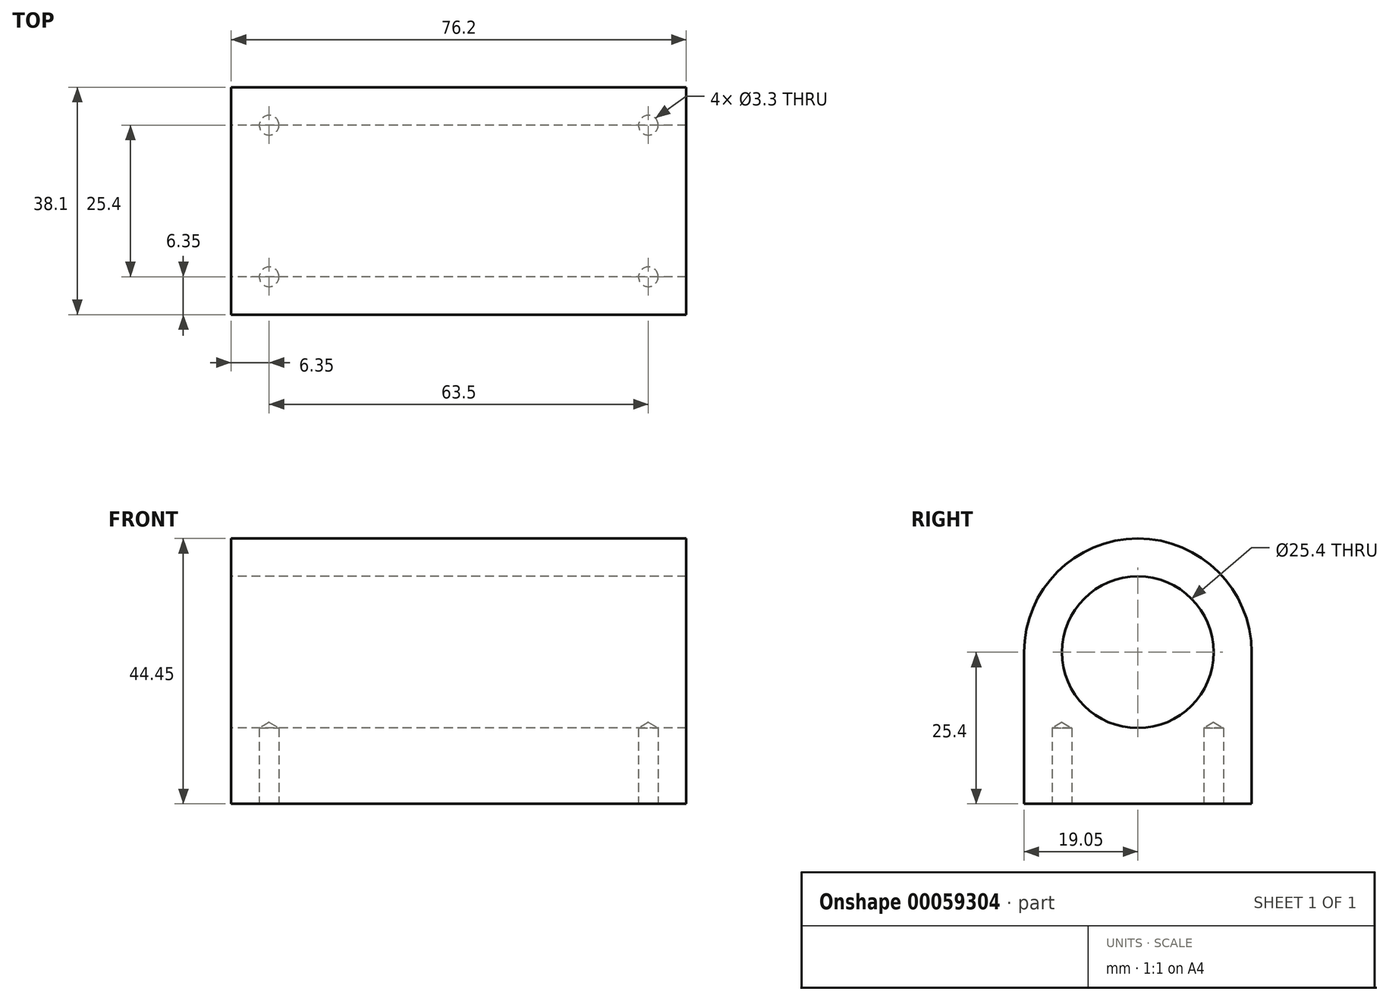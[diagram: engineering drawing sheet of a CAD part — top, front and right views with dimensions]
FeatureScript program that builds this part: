
annotation { "Feature Type Name" : "Feature", "Feature Type Description" : "" }
export const myFeature = defineFeature(function(context is Context, id is Id, definition is map)
    precondition{}
    {
        {
            var Q0;
            Q0=qCreatedBy(makeId("Right.planeOp"),FACE);
            var sketch = newSketch(context, id + "F0", { "sketchPlane" : qUnion([Q0])});
            skCircle(sketch, "E0", {"center": v(0, 0) * mm, "radius": 12.7 * mm});
            skArc(sketch, "E1", {"start": v(19.05, 0) * mm, "mid": v(0, 19.05) * mm, "end": v(-19.05, 0) * mm});
            skLineSegment(sketch, "E2", {"start": v(-19.05, 0) * mm, "end": v(-19.05, -25.4) * mm});
            skLineSegment(sketch, "E3", {"start": v(-19.05, -25.4) * mm, "end": v(19.05, -25.4) * mm});
            skLineSegment(sketch, "E4", {"start": v(19.05, 0) * mm, "end": v(19.05, -25.4) * mm});
            skSolve(sketch);
        }
        {
            var Q0;
            Q0=makeQuery(id+"F0.imprint","IMPRINT",FACE,{"disambiguationData":[TD([[makeQuery(id+"F0.imprint","IMPRINT",EDGE,{"derivedFrom":sQuery(id+"F0.wireOp",EDGE,"E0")}),-1.0]])]});
            extrude(context, id + "F1", {"entities" : qUnion([Q0]), "depth" : 76.2 * mm});
        }
        {
            var Q0;
            Q0=makeQuery(id+"F1.opExtrude","SWEPT_FACE",FACE,{"disambiguationData":[OSD([sQuery(id+"F0.wireOp",EDGE,"E3")])]});
            var sketch = newSketch(context, id + "F2", { "sketchPlane" : qUnion([Q0])});
            skSolve(sketch);
        }
        {
            var Q0;
            {var subQ0=sQuery(id+"F0.wireOp",EDGE,"E3");Q0=makeQuery(id+"F2.imprint","IMPRINT",FACE,{"disambiguationData":[TD([[makeQuery(id+"F2.imprint","IMPRINT",EDGE,{"derivedFrom":makeQuery(id+"F1.opExtrude","CAP_EDGE",EDGE,{"disambiguationData":[OSD([subQ0])],"isStart":true})}),1.0]])]});}
            var sketch = newSketch(context, id + "F3", { "sketchPlane" : qUnion([Q0])});
            skCircle(sketch, "E5", {"center": v(6.35, 12.7) * mm, "radius": 1.65 * mm});
            skCircle(sketch, "E6", {"center": v(6.35, -12.7) * mm, "radius": 1.65 * mm});
            skCircle(sketch, "E7", {"center": v(69.85, -12.7) * mm, "radius": 1.65 * mm});
            skCircle(sketch, "E8", {"center": v(69.85, 12.7) * mm, "radius": 1.65 * mm});
            skSolve(sketch);
        }
        {
            var Q0;
            Q0=sQuery(id+"F3.wireOp",VERTEX,"E5.center");
            var Q1;
            Q1=sQuery(id+"F3.wireOp",VERTEX,"E6.center");
            var Q2;
            Q2=sQuery(id+"F3.wireOp",VERTEX,"E7.center");
            var Q3;
            Q3=sQuery(id+"F3.wireOp",VERTEX,"E8.center");
            var Q4;
            Q4=makeQuery(id+"F1.opExtrude","SWEPT_BODY",BODY,{"disambiguationData":[OSD([sQuery(id+"F0.wireOp",EDGE,"E0"),sQuery(id+"F0.wireOp",EDGE,"E1"),sQuery(id+"F0.wireOp",EDGE,"E2"),sQuery(id+"F0.wireOp",EDGE,"E3"),sQuery(id+"F0.wireOp",EDGE,"E4")])]});
            hole(context, id + "F4", {"style" : HoleStyle.SIMPLE, "holeDiameter" : 3.3 * mm, "endStyle" : HoleEndStyle.BLIND, "holeDepth" : 12.7 * mm, "locations" : qUnion([Q0, Q1, Q2, Q3]), "scope" : qUnion([Q4])});
        }
    });
